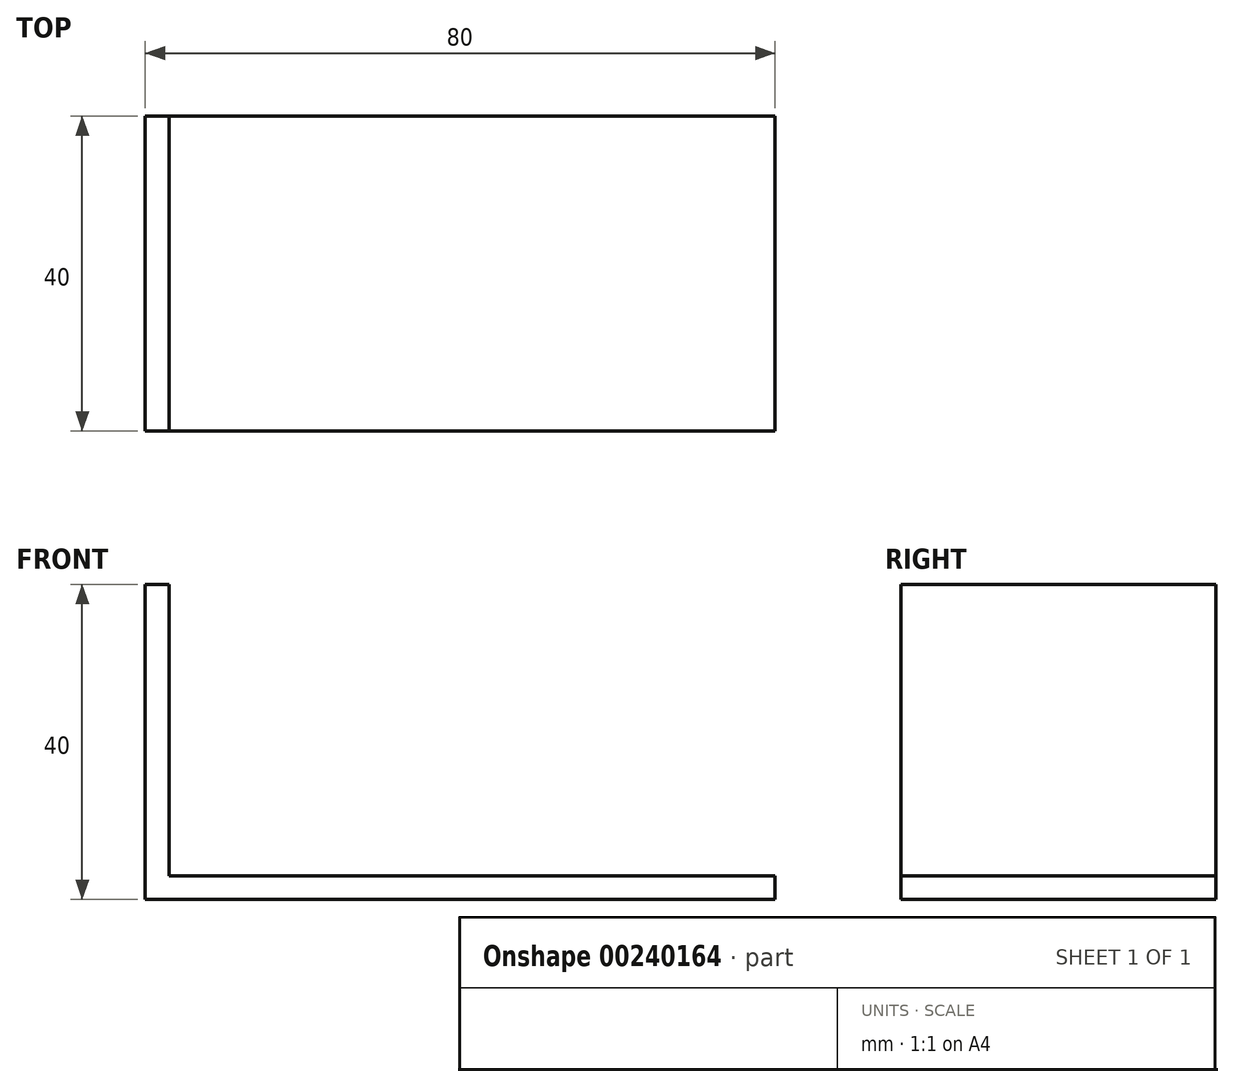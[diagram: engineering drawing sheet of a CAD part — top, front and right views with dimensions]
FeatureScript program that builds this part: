
annotation { "Feature Type Name" : "Feature", "Feature Type Description" : "" }
export const myFeature = defineFeature(function(context is Context, id is Id, definition is map)
    precondition{}
    {
        {
            var Q0;
            Q0=qCreatedBy(makeId("Front.planeOp"),FACE);
            var sketch = newSketch(context, id + "F0", { "sketchPlane" : qUnion([Q0])});
            skLineSegment(sketch, "E0", {"start": v(0, 0) * mm, "end": v(0, 40) * mm});
            skLineSegment(sketch, "E1", {"start": v(0, 0) * mm, "end": v(80, 0) * mm});
            skLineSegment(sketch, "E2.0", {"start": v(3, 3) * mm, "end": v(80, 3) * mm});
            skLineSegment(sketch, "E3", {"start": v(80, 0) * mm, "end": v(80, 3) * mm});
            skLineSegment(sketch, "E4.0", {"start": v(3, 3) * mm, "end": v(3, 40) * mm});
            skLineSegment(sketch, "E5", {"start": v(0, 40) * mm, "end": v(3, 40) * mm});
            skSolve(sketch);
        }
        {
            var Q0;
            Q0=makeQuery(id+"F0.imprint","IMPRINT",FACE,{"disambiguationData":[TD([[makeQuery(id+"F0.imprint","IMPRINT",EDGE,{"derivedFrom":sQuery(id+"F0.wireOp",EDGE,"E0")}),-1.0]])]});
            extrude(context, id + "F1", {"entities" : qUnion([Q0]), "oppositeDirection" : true, "depth" : 40 * mm});
        }
    });
